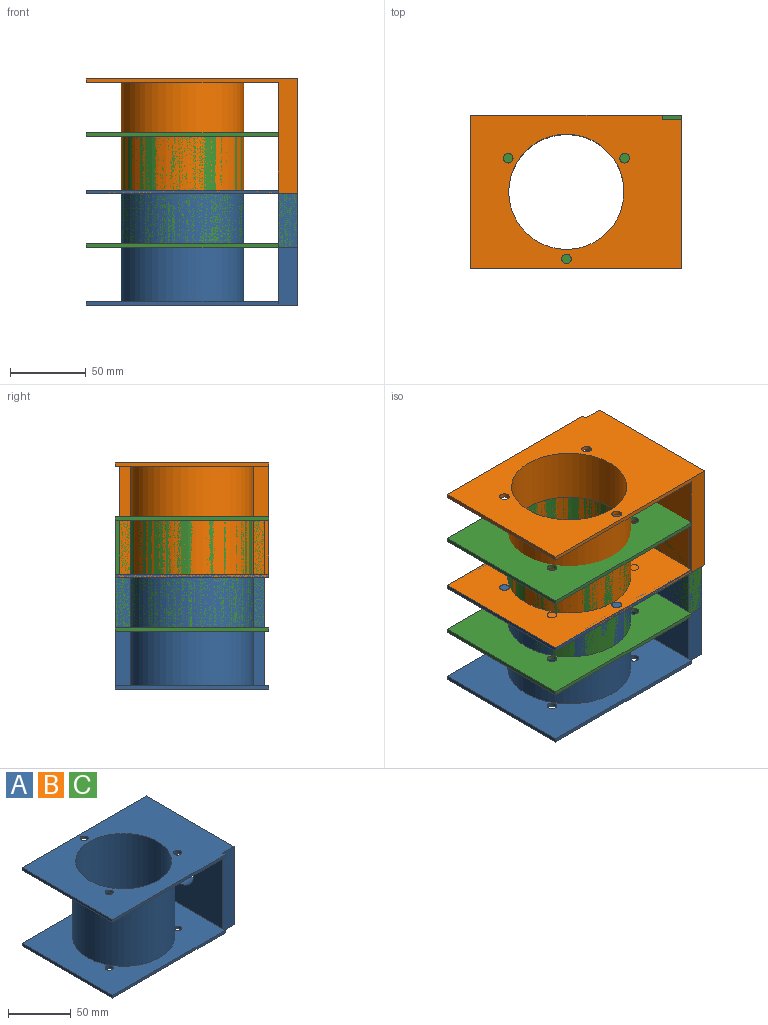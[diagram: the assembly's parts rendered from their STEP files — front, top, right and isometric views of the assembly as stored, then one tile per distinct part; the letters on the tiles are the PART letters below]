
ASSEMBLY  parts=3 mates=2
PART A: 23 faces, bbox 139.7x101.6x76.2 mm
  f0: plane 2.84x2.54mm, normal (1,0,0), area 7.2mm2, adj f5,f7,f10,f20
  f1: plane 2.84x2.54mm, normal (1,0,0), area 7.2mm2, adj f2,f6,f11,f20
  f2: plane 127x2.54mm, normal (0,-1,0), area 322.6mm2, adj f1,f4,f6,f11
  f3: plane 101.6x2.54mm, normal (-1,0,0), area 258.1mm2, adj f5,f7,f8,f10
  f4: plane 101.6x2.54mm, normal (-1,0,0), area 258.1mm2, adj f2,f6,f8,f11
  f5: plane 139.7x101.6mm, normal (0,0,-1), area 9502.1mm2, adj f0,f3,f7,f8,f9,f16,f17,f18
  f6: plane 139.7x101.6mm, normal (0,0,1), area 9502.1mm2, adj f1,f2,f4,f8,f9,f13,f14,f15
  f7: plane 127x2.54mm, normal (0,-1,0), area 322.6mm2, adj f0,f3,f5,f10
  f8: plane 139.7x76.2mm, normal (0,1,0), area 1612.9mm2, adj f3,f4,f5,f6,f10,f11,f19,f21
  f9: cylinder r=38.1mm len=76.2mm, axis (0,0,1), area 18241.5mm2, adj f5,f6
  f10: plane 127x101.6mm, normal (0,0,1), area 7619.5mm2, adj f0,f3,f7,f8,f12,f16,f17,f18
  f11: plane 127x101.6mm, normal (0,0,-1), area 7619.5mm2, adj f1,f2,f4,f8,f12,f13,f14,f15
  f12: cylinder r=40.64mm len=81.28mm, axis (0,0,1), area 18160.4mm2, adj f10,f11
  f13: cylinder r=3.17mm len=6.35mm, axis (0,0,1), area 50.7mm2, adj f6,f11
  f14: cylinder r=3.17mm len=6.35mm, axis (0,0,1), area 50.7mm2, adj f6,f11
  f15: cylinder r=3.17mm len=6.35mm, axis (0,0,1), area 50.7mm2, adj f6,f11
  f16: cylinder r=3.17mm len=6.35mm, axis (0,0,1), area 50.7mm2, adj f5,f10
  f17: cylinder r=3.17mm len=6.35mm, axis (0,0,1), area 50.7mm2, adj f5,f10
  f18: cylinder r=3.17mm len=6.35mm, axis (0,0,1), area 50.7mm2, adj f5,f10
  f19: plane 98.76x71.12mm, normal (-1,0,0), area 6297.6mm2, adj f8,f10,f11,f20,f22
  f20: plane 76.2x12.7mm, normal (0,-1,0), area 967.7mm2, adj f0,f1,f5,f6,f19,f21
  f21: plane 98.76x76.2mm, normal (1,0,0), area 6799.3mm2, adj f5,f6,f8,f20,f22
  f22: cylinder r=15.2mm len=30.41mm, axis (1,0,0), area 1213.1mm2, adj f19,f21
PART B: same geometry as A
PART C: same geometry as A
PLACE A t=(-119.44,88.82,-36.79)mm
PLACE B rot(axis=(1,0,0),180deg) t=(-119.44,88.82,36.87)mm
PLACE C t=(-119.44,88.82,1.31)mm fixed
MATE fastened C.f9 <-> B.f9  axis (0,0,1) through (-119.44,88.82,1.31)mm
MATE fastened B.f9 <-> A.f9  axis (0,0,-1) through (-119.44,88.82,-1.23)mm
